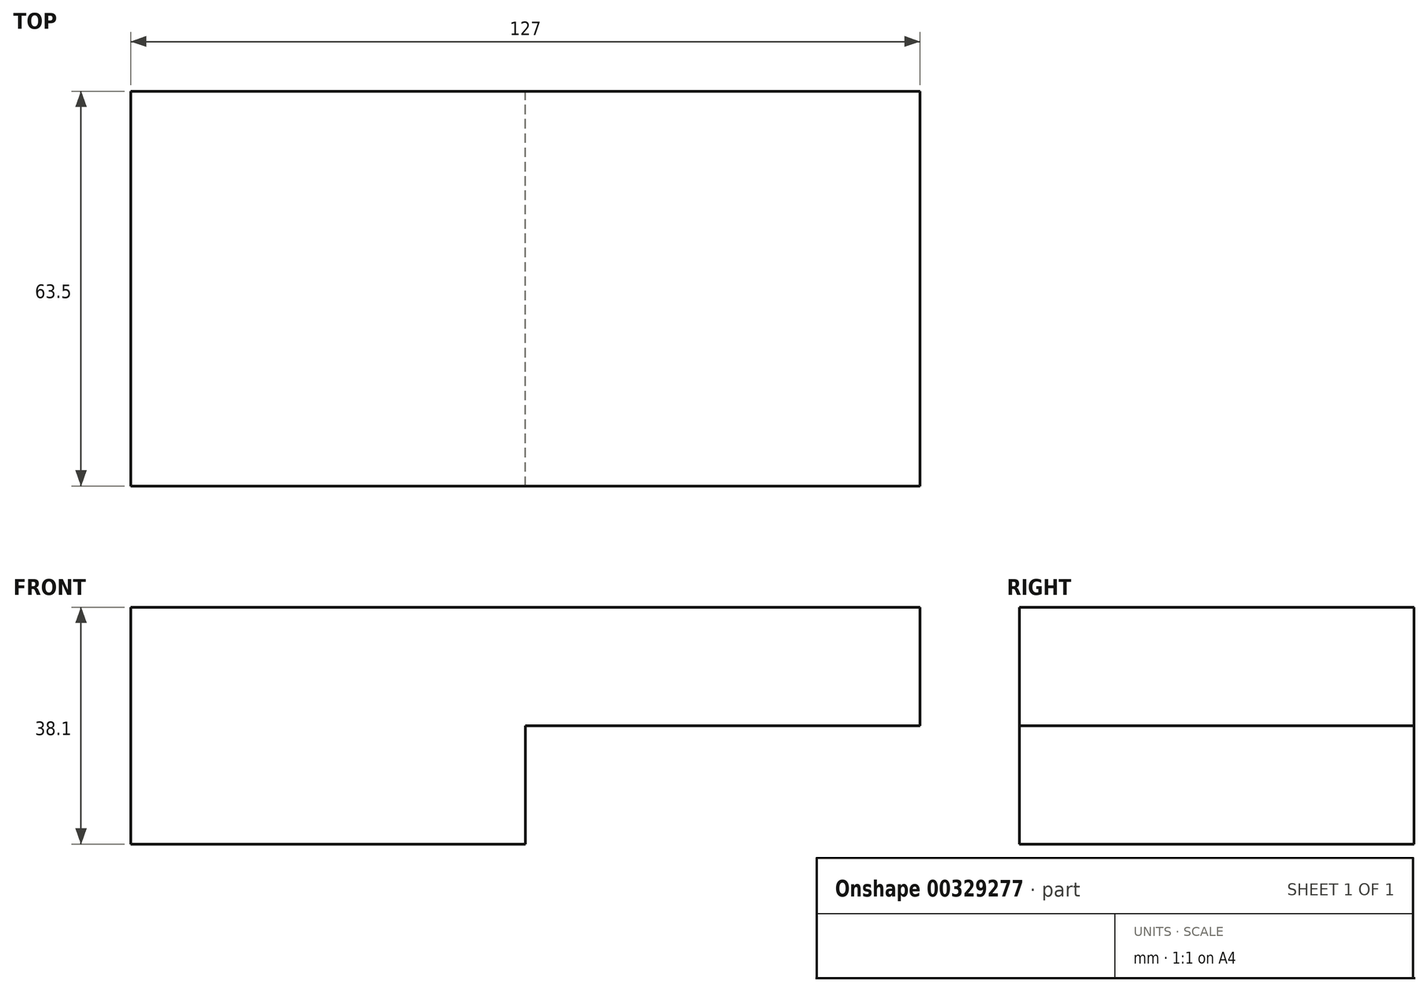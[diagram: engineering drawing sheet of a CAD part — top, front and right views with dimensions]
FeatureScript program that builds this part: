
annotation { "Feature Type Name" : "Feature", "Feature Type Description" : "" }
export const myFeature = defineFeature(function(context is Context, id is Id, definition is map)
    precondition{}
    {
        {
            var Q0;
            Q0=qCreatedBy(makeId("Front.planeOp"),FACE);
            var sketch = newSketch(context, id + "F0", { "sketchPlane" : qUnion([Q0])});
            skLineSegment(sketch, "E0", {"start": v(-58.38, 43.98) * mm, "end": v(68.62, 43.98) * mm});
            skLineSegment(sketch, "E1", {"start": v(-58.38, 43.98) * mm, "end": v(-58.38, 5.88) * mm});
            skLineSegment(sketch, "E2", {"start": v(-58.38, 5.88) * mm, "end": v(5.12, 5.88) * mm});
            skLineSegment(sketch, "E3", {"start": v(5.12, 5.88) * mm, "end": v(5.12, 24.93) * mm});
            skLineSegment(sketch, "E4", {"start": v(5.12, 24.93) * mm, "end": v(68.62, 24.93) * mm});
            skLineSegment(sketch, "E5", {"start": v(68.62, 43.98) * mm, "end": v(68.62, 24.93) * mm});
            skSolve(sketch);
        }
        {
            var Q0;
            Q0 = qSketchRegion(id + "F0", true);
            extrude(context, id + "F1", {"entities" : qUnion([Q0]), "depth" : 63.5 * mm});
        }
    });
